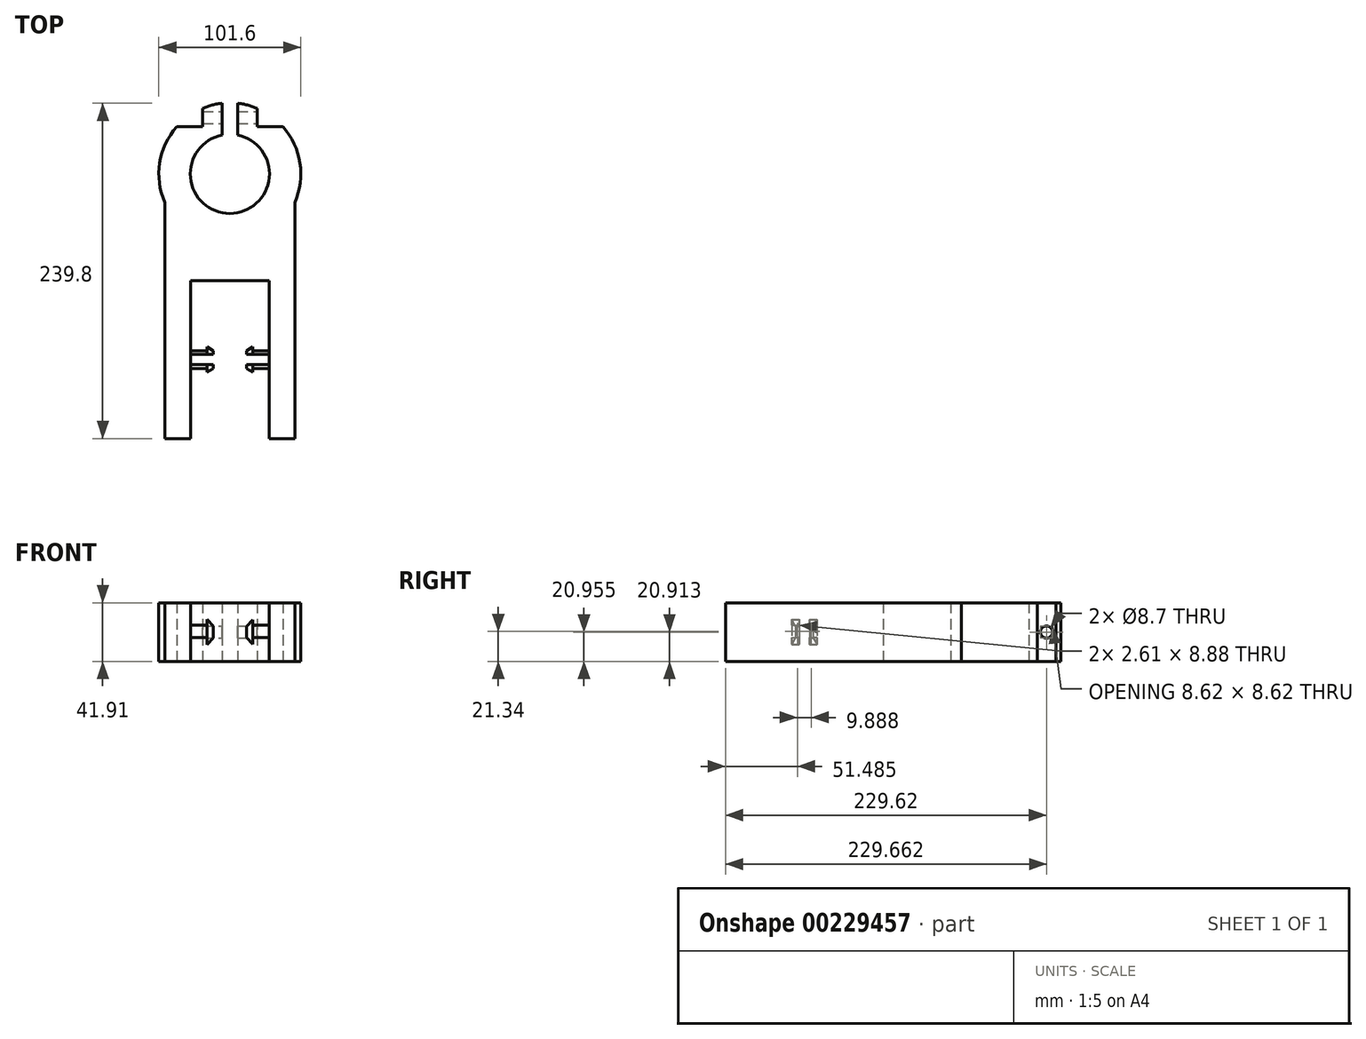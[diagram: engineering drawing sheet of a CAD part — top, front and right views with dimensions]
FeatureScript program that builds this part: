
annotation { "Feature Type Name" : "Feature", "Feature Type Description" : "" }
export const myFeature = defineFeature(function(context is Context, id is Id, definition is map)
    precondition{}
    {
        {
            var Q0;
            Q0=qCreatedBy(makeId("Top.planeOp"),FACE);
            var sketch = newSketch(context, id + "F0", { "sketchPlane" : qUnion([Q0])});
            skArc(sketch, "E0", {"start": v(-5.46, 27.79) * mm, "mid": v(0, -28.32) * mm, "end": v(5.46, 27.79) * mm});
            skArc(sketch, "E1", {"start": v(-37.98, 33.74) * mm, "mid": v(-50.2, 7.84) * mm, "end": v(-46.46, -20.55) * mm});
            skLineSegment(sketch, "E2", {"start": v(-19.47, 46.92) * mm, "end": v(-19.47, 33.74) * mm});
            skLineSegment(sketch, "E3.MirrorCS", {"start": v(19.47, 46.92) * mm, "end": v(19.47, 33.74) * mm});
            skLineSegment(sketch, "E4", {"start": v(-19.47, 33.74) * mm, "end": v(-37.98, 33.74) * mm});
            skLineSegment(sketch, "E5.MirrorCS", {"start": v(19.47, 33.74) * mm, "end": v(37.98, 33.74) * mm});
            skArc(sketch, "E6.trimOffspring", {"start": v(19.47, 46.92) * mm, "mid": v(12.6, 49.21) * mm, "end": v(5.46, 50.5) * mm});
            skLineSegment(sketch, "E7", {"start": v(-5.46, 50.5) * mm, "end": v(-5.46, 27.79) * mm});
            skLineSegment(sketch, "E8.MirrorCS", {"start": v(5.46, 50.5) * mm, "end": v(5.46, 27.79) * mm});
            skArc(sketch, "E9.trimOffspring", {"start": v(-5.46, 50.5) * mm, "mid": v(-12.6, 49.21) * mm, "end": v(-19.47, 46.92) * mm});
            skLineSegment(sketch, "E10", {"start": v(-46.46, -20.55) * mm, "end": v(-46.46, -189.3) * mm});
            skLineSegment(sketch, "E11", {"start": v(-46.46, -189.3) * mm, "end": v(-28.02, -189.3) * mm});
            skLineSegment(sketch, "E12.MirrorCS", {"start": v(46.46, -20.55) * mm, "end": v(46.46, -189.3) * mm});
            skLineSegment(sketch, "E13.MirrorCS", {"start": v(46.46, -189.3) * mm, "end": v(28.02, -189.3) * mm});
            skLineSegment(sketch, "E14", {"start": v(-28.02, -189.3) * mm, "end": v(-28.02, -139.1) * mm});
            skLineSegment(sketch, "E15", {"start": v(-28.02, -76.43) * mm, "end": v(0, -76.43) * mm});
            skLineSegment(sketch, "E16.MirrorCS", {"start": v(28.02, -76.43) * mm, "end": v(0, -76.43) * mm});
            skLineSegment(sketch, "E17.MirrorCS", {"start": v(28.02, -189.3) * mm, "end": v(28.02, -139.1) * mm});
            skPoint(sketch, "E18.orphan", {"position": v(0, -189.3) * mm});
            skPoint(sketch, "E19.endSnap0", {"position": v(-28.02, -132.86) * mm});
            skLineSegment(sketch, "E20", {"start": v(-28.02, -136.5) * mm, "end": v(-16.36, -136.5) * mm});
            skLineSegment(sketch, "E21", {"start": v(-16.36, -136.5) * mm, "end": v(-11.98, -136.5) * mm});
            skLineSegment(sketch, "E22", {"start": v(-11.98, -136.5) * mm, "end": v(-11.98, -139.2) * mm});
            skLineSegment(sketch, "E23", {"start": v(-11.98, -139.2) * mm, "end": v(-16.36, -141.9) * mm});
            skLineSegment(sketch, "E24", {"start": v(-16.36, -141.9) * mm, "end": v(-16.36, -139.1) * mm});
            skLineSegment(sketch, "E25", {"start": v(-16.36, -139.1) * mm, "end": v(-28.02, -139.1) * mm});
            skLineSegment(sketch, "E26.MirrorCS", {"start": v(-16.36, -129.22) * mm, "end": v(-11.98, -129.22) * mm});
            skLineSegment(sketch, "E27.MirrorCS", {"start": v(-28.02, -129.22) * mm, "end": v(-16.36, -129.22) * mm});
            skLineSegment(sketch, "E28.MirrorCS", {"start": v(-16.36, -126.61) * mm, "end": v(-28.02, -126.61) * mm});
            skLineSegment(sketch, "E29.MirrorCS", {"start": v(-16.36, -123.83) * mm, "end": v(-16.36, -126.61) * mm});
            skLineSegment(sketch, "E30.MirrorCS", {"start": v(-11.98, -126.52) * mm, "end": v(-16.36, -123.83) * mm});
            skLineSegment(sketch, "E31.MirrorCS", {"start": v(-11.98, -129.22) * mm, "end": v(-11.98, -126.52) * mm});
            skLineSegment(sketch, "E32.trimOffspring", {"start": v(-28.02, -126.61) * mm, "end": v(-28.02, -76.43) * mm});
            skLineSegment(sketch, "E33.trimOffspring", {"start": v(-28.02, -136.5) * mm, "end": v(-28.02, -129.22) * mm});
            skLineSegment(sketch, "E34.MirrorCS", {"start": v(11.98, -129.22) * mm, "end": v(11.98, -126.52) * mm});
            skLineSegment(sketch, "E35.MirrorCS", {"start": v(11.98, -126.52) * mm, "end": v(16.36, -123.83) * mm});
            skLineSegment(sketch, "E36.MirrorCS", {"start": v(16.36, -123.83) * mm, "end": v(16.36, -126.61) * mm});
            skLineSegment(sketch, "E37.MirrorCS", {"start": v(16.36, -126.61) * mm, "end": v(28.02, -126.61) * mm});
            skLineSegment(sketch, "E38.MirrorCS", {"start": v(28.02, -129.22) * mm, "end": v(16.36, -129.22) * mm});
            skLineSegment(sketch, "E39.MirrorCS", {"start": v(16.36, -129.22) * mm, "end": v(11.98, -129.22) * mm});
            skLineSegment(sketch, "E40.MirrorCS", {"start": v(11.98, -136.5) * mm, "end": v(11.98, -139.2) * mm});
            skLineSegment(sketch, "E41.MirrorCS", {"start": v(16.36, -136.5) * mm, "end": v(11.98, -136.5) * mm});
            skLineSegment(sketch, "E42.MirrorCS", {"start": v(28.02, -136.5) * mm, "end": v(16.36, -136.5) * mm});
            skLineSegment(sketch, "E43.MirrorCS", {"start": v(16.36, -139.1) * mm, "end": v(28.02, -139.1) * mm});
            skLineSegment(sketch, "E44.MirrorCS", {"start": v(11.98, -139.2) * mm, "end": v(16.36, -141.9) * mm});
            skLineSegment(sketch, "E45.MirrorCS", {"start": v(16.36, -141.9) * mm, "end": v(16.36, -139.1) * mm});
            skLineSegment(sketch, "E46.trimOffspring", {"start": v(28.02, -126.61) * mm, "end": v(28.02, -76.43) * mm});
            skLineSegment(sketch, "E47.trimOffspring", {"start": v(28.02, -136.5) * mm, "end": v(28.02, -129.22) * mm});
            skPoint(sketch, "E19.end.orphan", {"position": v(-17.37, -132.86) * mm});
            skPoint(sketch, "E19.start.orphan", {"position": v(-28.02, -132.86) * mm});
            skArc(sketch, "E48.trimOffspring", {"start": v(46.46, -20.55) * mm, "mid": v(50.2, 7.84) * mm, "end": v(37.98, 33.74) * mm});
            skPoint(sketch, "E49.orphan", {"position": v(19.47, 20.56) * mm});
            skPoint(sketch, "E50.orphan", {"position": v(-19.47, 20.56) * mm});
            skSolve(sketch);
        }
        {
            var Q0;
            Q0=makeQuery(id+"F0.imprint","IMPRINT",FACE,{"disambiguationData":[TD([[makeQuery(id+"F0.imprint","IMPRINT",EDGE,{"derivedFrom":sQuery(id+"F0.wireOp",EDGE,"E0")}),-1.0]])]});
            extrude(context, id + "F1", {"entities" : qUnion([Q0]), "depth" : 41.9 * mm});
        }
        {
            var Q0;
            Q0=makeQuery(id+"F1.opExtrude","SWEPT_FACE",FACE,{"disambiguationData":[OSD([sQuery(id+"F0.wireOp",EDGE,"E15"),sQuery(id+"F0.wireOp",EDGE,"E16.MirrorCS")])]});
            var sketch = newSketch(context, id + "F2", { "sketchPlane" : qUnion([Q0])});
            skLineSegment(sketch, "E51", {"start": v(-28.02, 29.98) * mm, "end": v(-28.02, 41.91) * mm});
            skLineSegment(sketch, "E52", {"start": v(-28.02, 41.91) * mm, "end": v(28.02, 41.91) * mm});
            skLineSegment(sketch, "E53", {"start": v(28.02, 41.91) * mm, "end": v(28.02, 29.98) * mm});
            skLineSegment(sketch, "E54", {"start": v(-28.02, 11.93) * mm, "end": v(-28.02, 0) * mm});
            skLineSegment(sketch, "E55", {"start": v(-28.02, 0) * mm, "end": v(28.02, 0) * mm});
            skLineSegment(sketch, "E56", {"start": v(28.02, 0) * mm, "end": v(28.02, 11.93) * mm});
            skPoint(sketch, "E57.end.orphan", {"position": v(-28.02, 20.96) * mm});
            skPoint(sketch, "E58.start.orphan", {"position": v(28.02, 20.96) * mm});
            skLineSegment(sketch, "E59", {"start": v(-16.32, 29.98) * mm, "end": v(-11.69, 25) * mm});
            skLineSegment(sketch, "E60", {"start": v(-11.69, 25) * mm, "end": v(12.1, 25) * mm});
            skLineSegment(sketch, "E61", {"start": v(12.1, 25) * mm, "end": v(16.53, 29.98) * mm});
            skLineSegment(sketch, "E62.MirrorCS", {"start": v(-11.69, 16.92) * mm, "end": v(12.1, 16.92) * mm});
            skLineSegment(sketch, "E63.MirrorCS", {"start": v(12.1, 16.92) * mm, "end": v(16.53, 11.93) * mm});
            skLineSegment(sketch, "E64.MirrorCS", {"start": v(-16.32, 11.93) * mm, "end": v(-11.69, 16.92) * mm});
            skLineSegment(sketch, "E65", {"start": v(-16.32, 29.98) * mm, "end": v(-16.32, 25.78) * mm});
            skLineSegment(sketch, "E66", {"start": v(-16.32, 25.78) * mm, "end": v(-28.02, 25.78) * mm});
            skLineSegment(sketch, "E67", {"start": v(-16.32, 11.93) * mm, "end": v(-16.32, 16.9) * mm});
            skLineSegment(sketch, "E68", {"start": v(-16.32, 16.9) * mm, "end": v(-28.02, 16.9) * mm});
            skLineSegment(sketch, "E69", {"start": v(0, 0) * mm, "end": v(0, 8.83) * mm});
            skPoint(sketch, "E69.endSnap0", {"position": v(0, 0) * mm});
            skLineSegment(sketch, "E70.MirrorCS", {"start": v(16.32, 16.9) * mm, "end": v(28.02, 16.9) * mm});
            skLineSegment(sketch, "E71.MirrorCS", {"start": v(16.32, 25.78) * mm, "end": v(28.02, 25.78) * mm});
            skLineSegment(sketch, "E72.MirrorCS", {"start": v(16.32, 11.93) * mm, "end": v(16.32, 16.9) * mm});
            skLineSegment(sketch, "E73.MirrorCS", {"start": v(16.32, 29.98) * mm, "end": v(16.32, 25.78) * mm});
            skSolve(sketch);
        }
        {
            var Q0;
            {var subQ2=sQuery(id+"F2.wireOp",EDGE,"E51");Q0=makeQuery(id+"F2.imprint","IMPRINT",FACE,{"disambiguationData":[TD([[makeQuery(id+"F2.imprint","IMPRINT",EDGE,{"derivedFrom":subQ2}),1.0]])]});}
            var Q1;
            {var subQ1=sQuery(id+"F2.wireOp",EDGE,"E54");Q1=makeQuery(id+"F2.imprint","IMPRINT",FACE,{"disambiguationData":[TD([[makeQuery(id+"F2.imprint","IMPRINT",EDGE,{"derivedFrom":subQ1}),1.0]])]});}
            extrude(context, id + "F3", {"entities" : qUnion([Q0, Q1]), "operationType" : NewBodyOperationType.REMOVE, "depth" : 132.84 * mm});
        }
        {
            var Q0;
            Q0=makeQuery(id+"F1.opExtrude","SWEPT_FACE",FACE,{"disambiguationData":[OSD([sQuery(id+"F0.wireOp",EDGE,"E3.MirrorCS")])]});
            var sketch = newSketch(context, id + "F4", { "sketchPlane" : qUnion([Q0])});
            skCircle(sketch, "E74", {"center": v(40.33, 20.96) * mm, "radius": 4.35 * mm});
            skPoint(sketch, "E74.centerSnap0", {"position": v(40.33, 41.91) * mm});
            skPoint(sketch, "E74.centerSnap1", {"position": v(33.74, 20.96) * mm});
            skSolve(sketch);
        }
        {
            var Q0;
            Q0=makeQuery(id+"F4.imprint","IMPRINT",FACE,{"disambiguationData":[TD([[makeQuery(id+"F4.imprint","IMPRINT",EDGE,{"derivedFrom":sQuery(id+"F4.wireOp",EDGE,"E74")}),1.0]])]});
            extrude(context, id + "F5", {"entities" : qUnion([Q0]), "operationType" : NewBodyOperationType.REMOVE, "oppositeDirection" : true, "depth" : 93 * mm});
        }
    });
